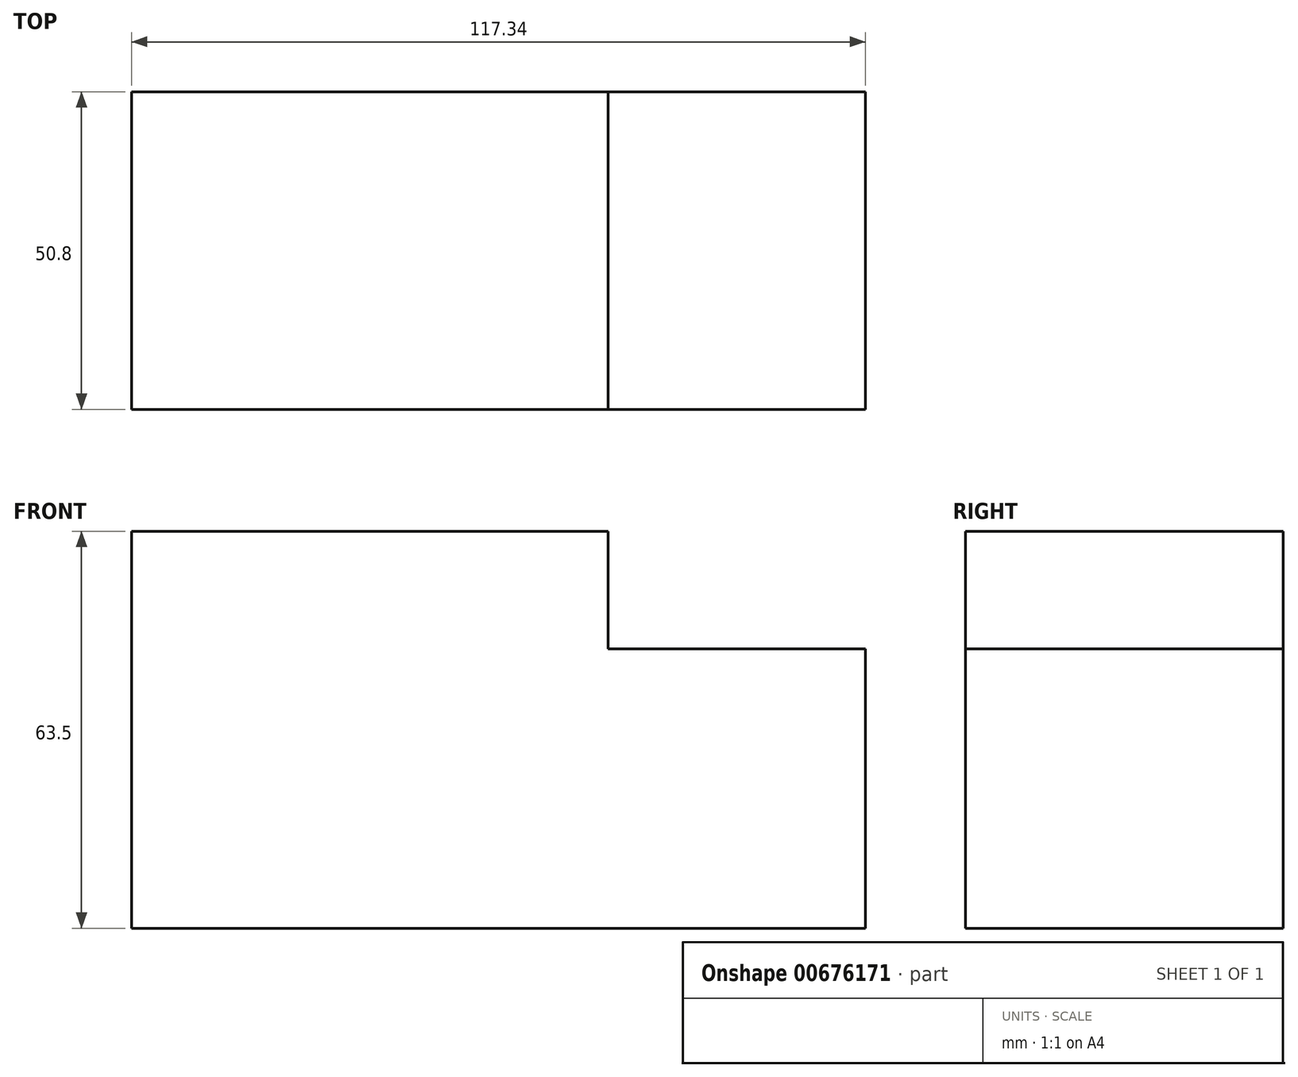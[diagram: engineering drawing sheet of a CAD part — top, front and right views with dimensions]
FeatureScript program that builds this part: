
annotation { "Feature Type Name" : "Feature", "Feature Type Description" : "" }
export const myFeature = defineFeature(function(context is Context, id is Id, definition is map)
    precondition{}
    {
        {
            var Q0;
            Q0=qCreatedBy(makeId("Front.planeOp"),FACE);
            var sketch = newSketch(context, id + "F0", { "sketchPlane" : qUnion([Q0])});
            skLineSegment(sketch, "E0.bottom", {"start": v(58.67, 31.75) * mm, "end": v(-58.67, 31.75) * mm});
            skLineSegment(sketch, "E0.top", {"start": v(58.67, -31.75) * mm, "end": v(-58.67, -31.75) * mm});
            skLineSegment(sketch, "E0.left", {"start": v(58.67, 31.75) * mm, "end": v(58.67, -31.75) * mm});
            skLineSegment(sketch, "E0.right", {"start": v(-58.67, 31.75) * mm, "end": v(-58.67, -31.75) * mm});
            skPoint(sketch, "E0.middle", {"position": v(0, 0) * mm});
            skSolve(sketch);
        }
        {
            var Q0;
            Q0=makeQuery(id+"F0.imprint","IMPRINT",FACE,{"disambiguationData":[TD([[makeQuery(id+"F0.imprint","IMPRINT",EDGE,{"derivedFrom":sQuery(id+"F0.wireOp",EDGE,"E0.bottom")}),1.0]])]});
            extrude(context, id + "F1", {"entities" : qUnion([Q0]), "depth" : 50.8 * mm, "offsetDistance" : 25.4 * mm});
        }
        {
            var Q0;
            Q0=makeQuery(id+"F1.opExtrude","CAP_FACE",FACE,{"disambiguationData":[OSD([sQuery(id+"F0.wireOp",EDGE,"E0.bottom"),sQuery(id+"F0.wireOp",EDGE,"E0.top"),sQuery(id+"F0.wireOp",EDGE,"E0.left"),sQuery(id+"F0.wireOp",EDGE,"E0.right")])],"isStart":false});
            var sketch = newSketch(context, id + "F2", { "sketchPlane" : qUnion([Q0])});
            skLineSegment(sketch, "E1.bottom", {"start": v(58.67, 31.75) * mm, "end": v(17.53, 31.75) * mm});
            skLineSegment(sketch, "E1.top", {"start": v(58.67, 12.95) * mm, "end": v(17.53, 12.95) * mm});
            skLineSegment(sketch, "E1.left", {"start": v(58.67, 31.75) * mm, "end": v(58.67, 12.95) * mm});
            skLineSegment(sketch, "E1.right", {"start": v(17.53, 31.75) * mm, "end": v(17.53, 12.95) * mm});
            skSolve(sketch);
        }
        {
            var Q0;
            Q0 = qSketchRegion(id + "F2", true);
            extrude(context, id + "F3", {"entities" : qUnion([Q0]), "operationType" : NewBodyOperationType.REMOVE, "endBound" : BoundingType.THROUGH_ALL, "oppositeDirection" : true, "depth" : 25.4 * mm, "offsetDistance" : 25.4 * mm});
        }
    });
